AUTODESK INVENTOR PART (.ipt)
format: ipt  version: 2024.2 (Build 282272000, 272)  size: 71,680 bytes
history: native  units: mm
features: reference x4, other x3, sketch x1
ambient origin geometry x8: Origin, YZ Plane, XZ Plane, XY Plane, X Axis, Y Axis, Z Axis, Center Point
feature tree (8):
  sketch  "Sketch1"
  reference  "Reference1"
  reference  "Reference2"
  reference  "Reference3"
  reference  "Reference4"
  other  "<userpath>\Desktop\scioly-robot-tour\Hardware\ipt\v4\v4assembly.iam"
  other  "v4assembly.iam"
  other  "v4chassisv2:1"
